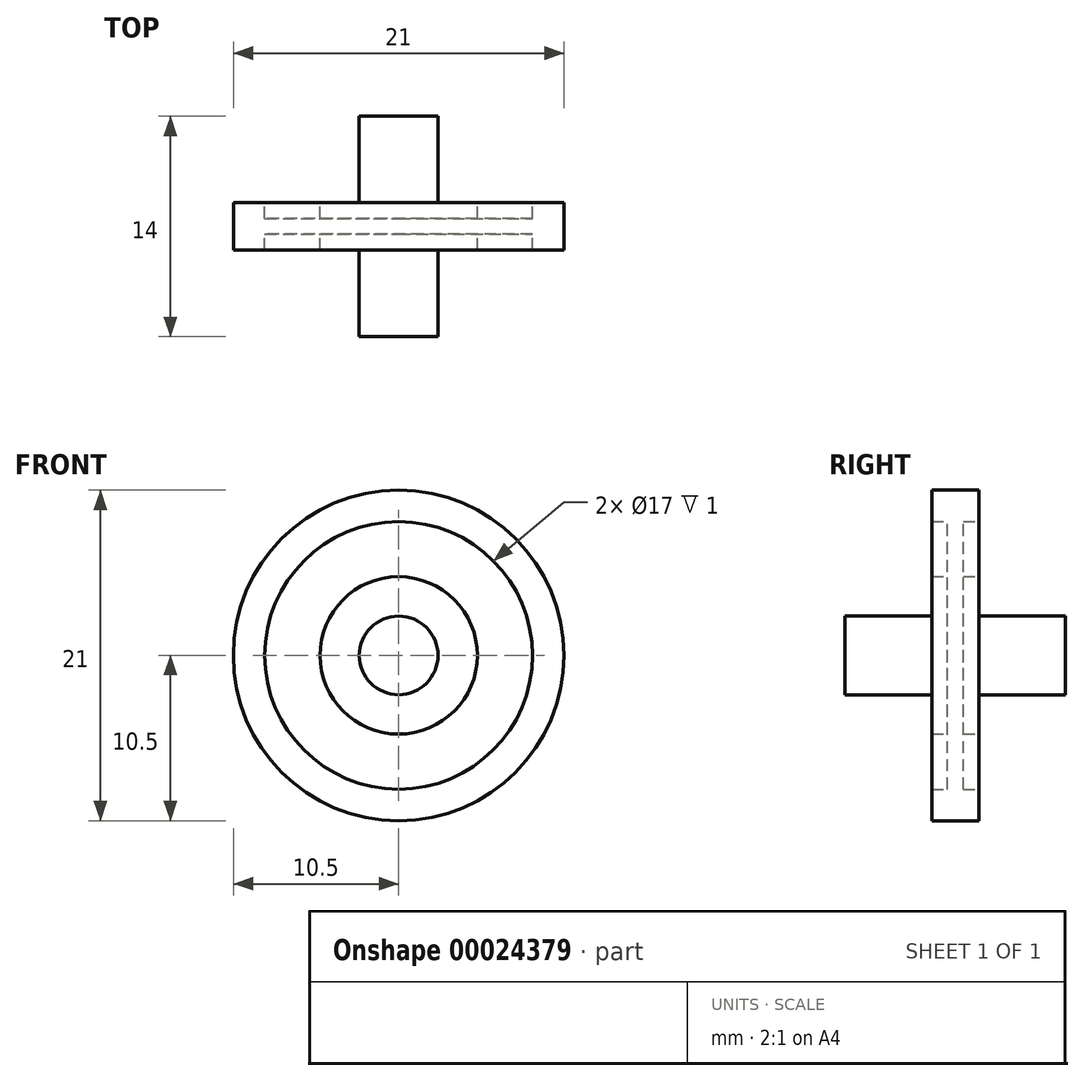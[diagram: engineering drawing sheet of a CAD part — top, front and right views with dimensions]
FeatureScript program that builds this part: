
annotation { "Feature Type Name" : "Feature", "Feature Type Description" : "" }
export const myFeature = defineFeature(function(context is Context, id is Id, definition is map)
    precondition{}
    {
        {
            var Q0;
            Q0=qCreatedBy(makeId("Front.planeOp"),FACE);
            var sketch = newSketch(context, id + "F0", { "sketchPlane" : qUnion([Q0])});
            skCircle(sketch, "E0", {"center": v(0, 0) * mm, "radius": 10.5 * mm});
            skCircle(sketch, "E1", {"center": v(0, 0) * mm, "radius": 8.5 * mm});
            skCircle(sketch, "E2", {"center": v(0, 0) * mm, "radius": 5 * mm});
            skCircle(sketch, "E3", {"center": v(0, 0) * mm, "radius": 2.5 * mm});
            skSolve(sketch);
        }
        {
            var Q0;
            Q0=makeQuery(id+"F0.imprint","IMPRINT",FACE,{"disambiguationData":[TD([[makeQuery(id+"F0.imprint","IMPRINT",EDGE,{"derivedFrom":sQuery(id+"F0.wireOp",EDGE,"E0")}),1.0]])]});
            extrude(context, id + "F1", {"entities" : qUnion([Q0]), "depth" : 1.5 * mm, "hasSecondDirection" : true, "secondDirectionOppositeDirection" : true, "secondDirectionDepth" : 1.5 * mm});
        }
        {
            var Q0;
            Q0=makeQuery(id+"F0.imprint","IMPRINT",FACE,{"disambiguationData":[TD([[makeQuery(id+"F0.imprint","IMPRINT",EDGE,{"derivedFrom":sQuery(id+"F0.wireOp",EDGE,"E1")}),1.0]])]});
            extrude(context, id + "F2", {"entities" : qUnion([Q0]), "operationType" : NewBodyOperationType.ADD, "depth" : 0.5 * mm, "hasSecondDirection" : true, "secondDirectionOppositeDirection" : true, "secondDirectionDepth" : 0.5 * mm});
        }
        {
            var Q0;
            Q0=makeQuery(id+"F0.imprint","IMPRINT",FACE,{"disambiguationData":[TD([[makeQuery(id+"F0.imprint","IMPRINT",EDGE,{"derivedFrom":sQuery(id+"F0.wireOp",EDGE,"E2")}),1.0]])]});
            extrude(context, id + "F3", {"entities" : qUnion([Q0]), "operationType" : NewBodyOperationType.ADD, "depth" : 1.5 * mm, "hasSecondDirection" : true, "secondDirectionOppositeDirection" : true, "secondDirectionDepth" : 1.5 * mm});
        }
        {
            var Q0;
            Q0=makeQuery(id+"F0.imprint","IMPRINT",FACE,{"disambiguationData":[TD([[makeQuery(id+"F0.imprint","IMPRINT",EDGE,{"derivedFrom":sQuery(id+"F0.wireOp",EDGE,"E3")}),1.0]])]});
            extrude(context, id + "F4", {"entities" : qUnion([Q0]), "operationType" : NewBodyOperationType.ADD, "endBound" : BoundingType.SYMMETRIC, "depth" : 14 * mm});
        }
    });
